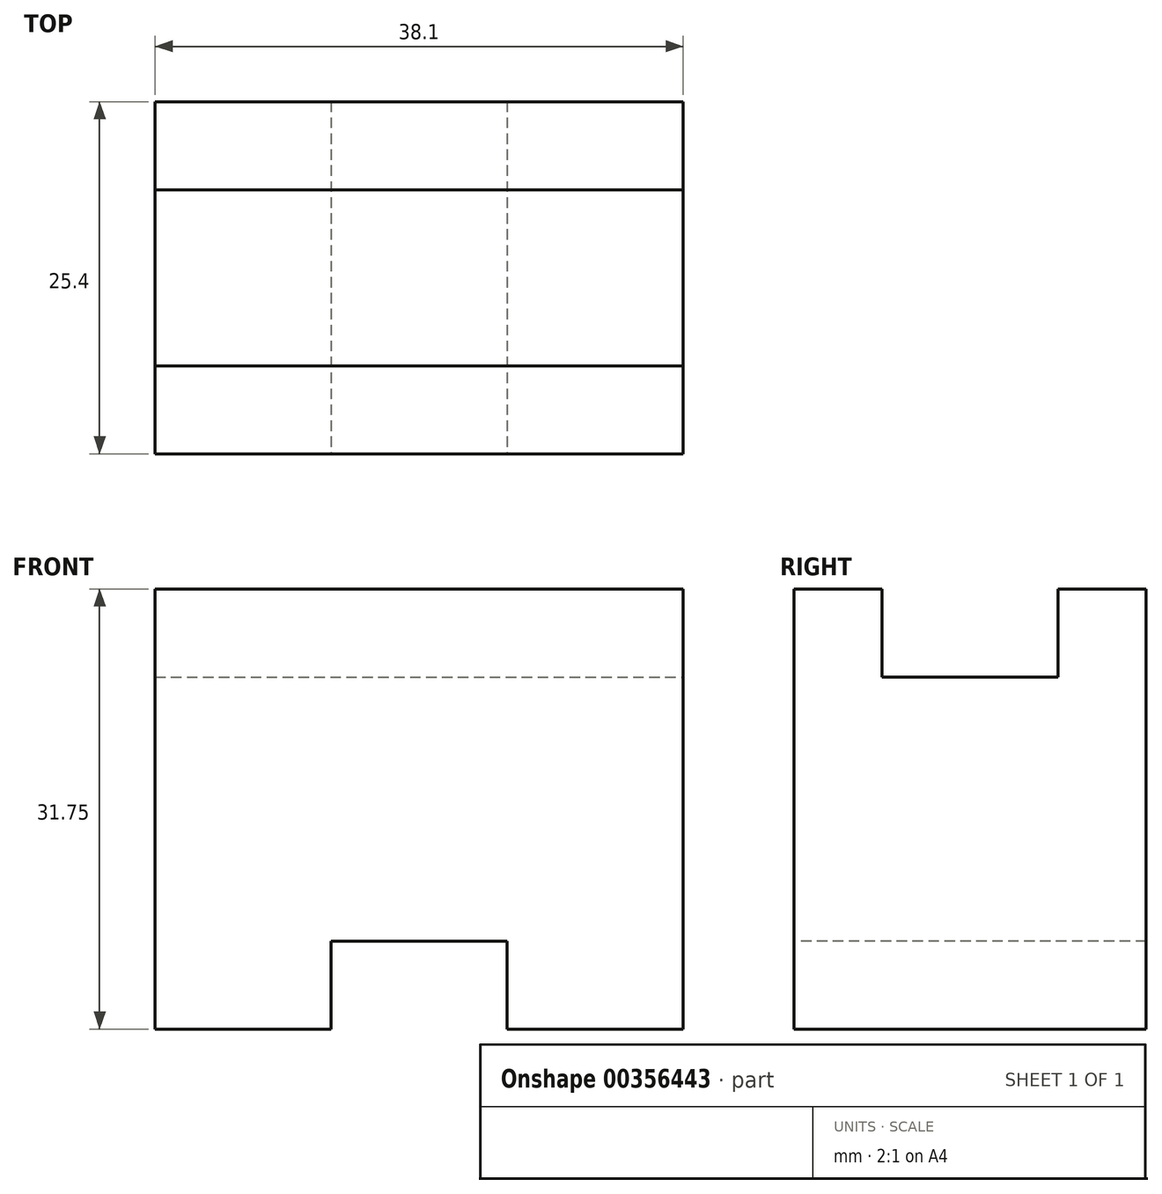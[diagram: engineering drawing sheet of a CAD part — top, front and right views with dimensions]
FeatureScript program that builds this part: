
annotation { "Feature Type Name" : "Feature", "Feature Type Description" : "" }
export const myFeature = defineFeature(function(context is Context, id is Id, definition is map)
    precondition{}
    {
        {
            var Q0;
            Q0=qCreatedBy(makeId("Right.planeOp"),FACE);
            var sketch = newSketch(context, id + "F0", { "sketchPlane" : qUnion([Q0])});
            skLineSegment(sketch, "E0", {"start": v(-12.34, 16.5) * mm, "end": v(-6, 16.5) * mm});
            skLineSegment(sketch, "E1", {"start": v(-6, 16.5) * mm, "end": v(-6, 10.15) * mm});
            skLineSegment(sketch, "E2", {"start": v(-6, 10.15) * mm, "end": v(6.7, 10.15) * mm});
            skLineSegment(sketch, "E3", {"start": v(6.7, 10.15) * mm, "end": v(6.7, 16.5) * mm});
            skLineSegment(sketch, "E4", {"start": v(6.7, 16.5) * mm, "end": v(13.06, 16.5) * mm});
            skLineSegment(sketch, "E5", {"start": v(13.06, 16.5) * mm, "end": v(13.06, -15.25) * mm});
            skLineSegment(sketch, "E6", {"start": v(-12.34, 16.5) * mm, "end": v(-12.34, -15.25) * mm});
            skLineSegment(sketch, "E7", {"start": v(-12.34, -15.25) * mm, "end": v(13.06, -15.25) * mm});
            skSolve(sketch);
        }
        {
            var Q0;
            Q0 = qSketchRegion(id + "F0", true);
            extrude(context, id + "F1", {"entities" : qUnion([Q0]), "oppositeDirection" : true, "depth" : 38.1 * mm});
        }
        {
            var Q0;
            Q0=makeQuery(id+"F1.opExtrude","SWEPT_FACE",FACE,{"disambiguationData":[OSD([sQuery(id+"F0.wireOp",EDGE,"E6")])]});
            var sketch = newSketch(context, id + "F2", { "sketchPlane" : qUnion([Q0])});
            skLineSegment(sketch, "E8", {"start": v(0, -15.25) * mm, "end": v(-12.7, -15.25) * mm});
            skLineSegment(sketch, "E9", {"start": v(-12.7, -15.25) * mm, "end": v(-12.7, -8.9) * mm});
            skLineSegment(sketch, "E10", {"start": v(-12.7, -8.9) * mm, "end": v(-25.4, -8.9) * mm});
            skLineSegment(sketch, "E11", {"start": v(-25.4, -8.9) * mm, "end": v(-25.4, -15.25) * mm});
            skLineSegment(sketch, "E12", {"start": v(-25.4, -15.25) * mm, "end": v(-12.7, -15.25) * mm});
            skSolve(sketch);
        }
        {
            var Q0;
            Q0 = qSketchRegion(id + "F2", true);
            extrude(context, id + "F3", {"entities" : qUnion([Q0]), "operationType" : NewBodyOperationType.REMOVE, "oppositeDirection" : true, "depth" : 25.4 * mm});
        }
    });
